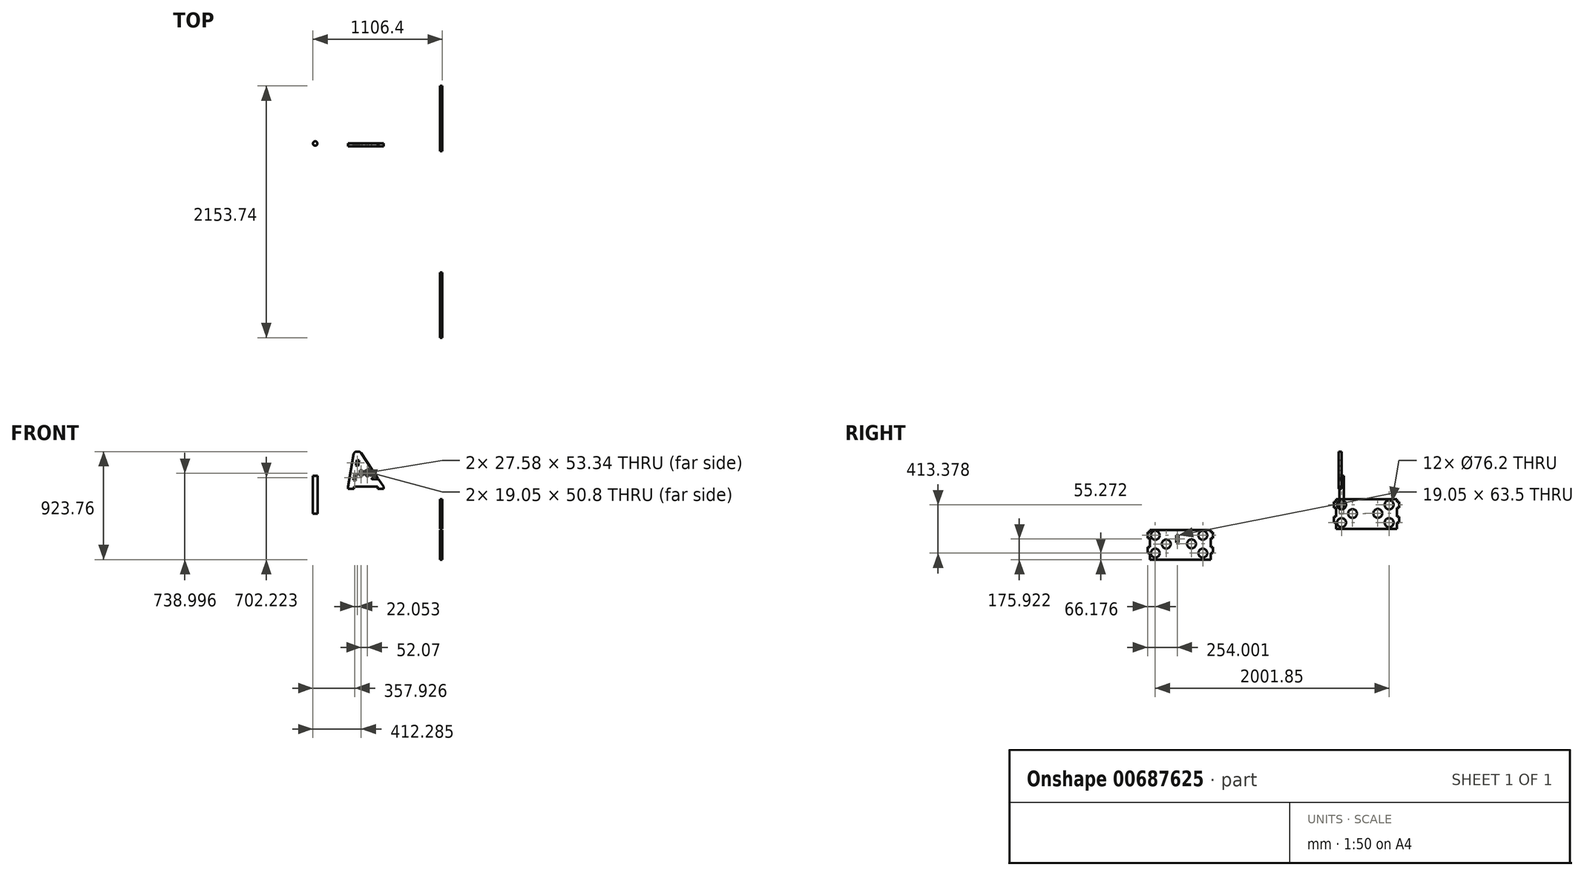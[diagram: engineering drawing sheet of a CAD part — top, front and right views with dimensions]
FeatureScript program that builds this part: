
annotation { "Feature Type Name" : "Feature", "Feature Type Description" : "" }
export const myFeature = defineFeature(function(context is Context, id is Id, definition is map)
    precondition{}
    {
        {
            var Q0;
            Q0=qCreatedBy(makeId("Front.planeOp"),FACE);
            var sketch = newSketch(context, id + "F0", { "sketchPlane" : qUnion([Q0])});
            skLineSegment(sketch, "E0", {"start": v(-737.52, 307.34) * mm, "end": v(-534.32, 307.34) * mm});
            skLineSegment(sketch, "E1", {"start": v(-788.32, 307.34) * mm, "end": v(-739.1, 586.52) * mm});
            skLineSegment(sketch, "E2", {"start": v(-714.08, 607.5) * mm, "end": v(-698.15, 607.5) * mm});
            skLineSegment(sketch, "E3", {"start": v(-677.04, 596.25) * mm, "end": v(-531.9, 379.57) * mm});
            skPoint(sketch, "E4.visualSharp", {"position": v(-735.39, 607.5) * mm});
            skArc(sketch, "E4.filletArc", {"start": v(-714.08, 607.5) * mm, "mid": v(-730.4, 601.57) * mm, "end": v(-739.1, 586.52) * mm});
            skPoint(sketch, "E5.visualSharp", {"position": v(-684.59, 607.5) * mm});
            skArc(sketch, "E5.filletArc", {"start": v(-677.04, 596.25) * mm, "mid": v(-686.19, 604.52) * mm, "end": v(-698.15, 607.5) * mm});
            skLineSegment(sketch, "E6", {"start": v(-712.34, 537.71) * mm, "end": v(-721.16, 487.68) * mm});
            skPoint(sketch, "E7", {"position": v(-738.8, 387.63) * mm});
            skPoint(sketch, "E8", {"position": v(-716.75, 512.7) * mm});
            skLineSegment(sketch, "E9", {"start": v(-715.63, 409.33) * mm, "end": v(-734.4, 412.64) * mm});
            skLineSegment(sketch, "E10.MirrorCS", {"start": v(-5.07, -152.24) * mm, "end": v(-5.07, -55.27) * mm});
            skLineSegment(sketch, "E11", {"start": v(-693.58, 534.4) * mm, "end": v(-712.34, 537.71) * mm});
            skLineSegment(sketch, "E12.MirrorCS", {"start": v(-702.4, 484.38) * mm, "end": v(-721.16, 487.68) * mm});
            skLineSegment(sketch, "E13.MirrorCS", {"start": v(-724.45, 359.3) * mm, "end": v(-743.22, 362.61) * mm});
            skLineSegment(sketch, "E14", {"start": v(-734.4, 412.64) * mm, "end": v(-743.22, 362.61) * mm});
            skPoint(sketch, "E15.orphan", {"position": v(-706.11, 607.5) * mm});
            skLineSegment(sketch, "E16.trimOffspring", {"start": v(-721.16, 487.68) * mm, "end": v(-716.75, 512.7) * mm});
            skPoint(sketch, "E17.orphan", {"position": v(-706.11, 307.34) * mm});
            skLineSegment(sketch, "E18.trimOffspring", {"start": v(-743.22, 362.61) * mm, "end": v(-734.4, 412.64) * mm});
            skLineSegment(sketch, "E19.0", {"start": v(-2.86, 20.83) * mm, "end": v(-2.86, 20.83) * mm});
            skLineSegment(sketch, "E19.1", {"start": v(-738.8, 387.63) * mm, "end": v(-716.75, 512.7) * mm, "construction": true});
            skLineSegment(sketch, "E19.9", {"start": v(-738.8, 387.63) * mm, "end": v(-734.4, 412.64) * mm, "construction": true});
            skLineSegment(sketch, "E20.0", {"start": v(-716.75, 512.7) * mm, "end": v(-712.34, 537.71) * mm, "construction": true});
            skPoint(sketch, "E21", {"position": v(-730.7, 360.4) * mm});
            skLineSegment(sketch, "E22", {"start": v(-693.58, 534.4) * mm, "end": v(-702.4, 484.38) * mm});
            skLineSegment(sketch, "E23", {"start": v(-715.63, 409.33) * mm, "end": v(-724.65, 358.2) * mm});
            skPoint(sketch, "E24.MirrorCS.end.orphan", {"position": v(-718.2, 358.2) * mm});
            skPoint(sketch, "E25.start.orphan", {"position": v(-743.22, 307.34) * mm});
            skPoint(sketch, "E26.end.orphan", {"position": v(-692.42, 288.03) * mm});
            skPoint(sketch, "E27.start.orphan", {"position": v(-576.67, 288.03) * mm});
            skPoint(sketch, "E28.start.orphan", {"position": v(-725.86, 288.3) * mm});
            skPoint(sketch, "E29.start.orphan", {"position": v(-549.17, 288.3) * mm});
            skLineSegment(sketch, "E30", {"start": v(-788.32, 307.34) * mm, "end": v(-788.32, 288.3) * mm});
            skLineSegment(sketch, "E31", {"start": v(-788.32, 288.3) * mm, "end": v(-737.52, 288.3) * mm});
            skLineSegment(sketch, "E32", {"start": v(-737.52, 288.3) * mm, "end": v(-737.52, 307.34) * mm});
            skLineSegment(sketch, "E33", {"start": v(-483.52, 307.34) * mm, "end": v(-483.52, 288.3) * mm});
            skLineSegment(sketch, "E34", {"start": v(-483.52, 288.3) * mm, "end": v(-534.32, 288.3) * mm});
            skLineSegment(sketch, "E35", {"start": v(-534.32, 288.3) * mm, "end": v(-534.32, 307.34) * mm});
            skPoint(sketch, "E36", {"position": v(-531.9, 379.57) * mm});
            skLineSegment(sketch, "E37", {"start": v(-531.9, 379.57) * mm, "end": v(-582.7, 379.57) * mm});
            skLineSegment(sketch, "E38", {"start": v(-585.24, 377.03) * mm, "end": v(-585.24, 374.31) * mm});
            skLineSegment(sketch, "E39", {"start": v(-582.7, 371.77) * mm, "end": v(-526.68, 371.77) * mm});
            skLineSegment(sketch, "E40.trimOffspring", {"start": v(-526.68, 371.77) * mm, "end": v(-483.52, 307.34) * mm});
            skPoint(sketch, "E41.visualSharp", {"position": v(-585.24, 379.57) * mm});
            skArc(sketch, "E41.filletArc", {"start": v(-582.7, 379.57) * mm, "mid": v(-584.5, 378.82) * mm, "end": v(-585.24, 377.03) * mm});
            skPoint(sketch, "E42.visualSharp", {"position": v(-585.24, 371.77) * mm});
            skArc(sketch, "E42.filletArc", {"start": v(-585.24, 374.31) * mm, "mid": v(-584.5, 372.52) * mm, "end": v(-582.7, 371.77) * mm});
            skLineSegment(sketch, "E43", {"start": v(-557.3, 379.57) * mm, "end": v(-585.24, 379.57) * mm});
            skLineSegment(sketch, "E44.top", {"start": v(-665.54, 448.15) * mm, "end": v(-684.59, 448.15) * mm});
            skLineSegment(sketch, "E44.left", {"start": v(-665.54, 397.35) * mm, "end": v(-665.54, 448.15) * mm});
            skLineSegment(sketch, "E44.right", {"start": v(-684.59, 397.35) * mm, "end": v(-684.59, 448.15) * mm});
            skLineSegment(sketch, "E45.trimOffspring", {"start": v(-665.54, 397.35) * mm, "end": v(-684.59, 397.35) * mm});
            skLineSegment(sketch, "E46.top", {"start": v(-613.47, 448.15) * mm, "end": v(-632.52, 448.15) * mm});
            skLineSegment(sketch, "E46.left", {"start": v(-613.47, 397.35) * mm, "end": v(-613.47, 448.15) * mm});
            skLineSegment(sketch, "E46.right", {"start": v(-632.52, 397.35) * mm, "end": v(-632.52, 448.15) * mm});
            skLineSegment(sketch, "E47.trimOffspring", {"start": v(-613.47, 397.35) * mm, "end": v(-632.52, 397.35) * mm});
            skSolve(sketch);
        }
        {
            var Q0;
            Q0=qCreatedBy(makeId("Right.planeOp"),FACE);
            var sketch = newSketch(context, id + "F1", { "sketchPlane" : qUnion([Q0])});
            skLineSegment(sketch, "E48.bottom", {"start": v(0, -58.22) * mm, "end": v(0, -58.22) * mm});
            skLineSegment(sketch, "E48.top", {"start": v(0, 410.3) * mm, "end": v(0, 410.3) * mm});
            skLineSegment(sketch, "E49.bottom", {"start": v(473.58, 198.73) * mm, "end": v(-47.12, 198.73) * mm});
            skLineSegment(sketch, "E49.top", {"start": v(473.58, -55.27) * mm, "end": v(-47.12, -55.27) * mm});
            skLineSegment(sketch, "E49.left", {"start": v(473.58, 198.73) * mm, "end": v(473.58, 50.8) * mm});
            skLineSegment(sketch, "E49.right", {"start": v(-47.12, 198.73) * mm, "end": v(-47.12, 177.8) * mm});
            skPoint(sketch, "E50", {"position": v(-47.12, 186.03) * mm});
            skPoint(sketch, "E51.MirrorP", {"position": v(-47.12, -38.1) * mm});
            skLineSegment(sketch, "E52", {"start": v(473.58, -55.27) * mm, "end": v(473.58, 0) * mm});
            skLineSegment(sketch, "E53", {"start": v(473.58, 0) * mm, "end": v(492.63, 0) * mm});
            skLineSegment(sketch, "E54", {"start": v(492.63, 0) * mm, "end": v(492.63, 50.8) * mm});
            skLineSegment(sketch, "E55", {"start": v(492.63, 50.8) * mm, "end": v(473.58, 50.8) * mm});
            skPoint(sketch, "E56", {"position": v(492.63, 25.4) * mm});
            skLineSegment(sketch, "E57.trimOffspring", {"start": v(473.58, 0) * mm, "end": v(473.58, -55.27) * mm});
            skLineSegment(sketch, "E58", {"start": v(473.58, 127) * mm, "end": v(492.63, 127) * mm});
            skLineSegment(sketch, "E59", {"start": v(492.63, 127) * mm, "end": v(492.63, 177.8) * mm});
            skLineSegment(sketch, "E60", {"start": v(492.63, 177.8) * mm, "end": v(473.58, 177.8) * mm});
            skPoint(sketch, "E61", {"position": v(492.63, 152.4) * mm});
            skLineSegment(sketch, "E62", {"start": v(213.23, 198.73) * mm, "end": v(213.23, -55.27) * mm});
            skLineSegment(sketch, "E63.MirrorCS", {"start": v(-47.12, 127) * mm, "end": v(-66.17, 127) * mm});
            skLineSegment(sketch, "E64.MirrorCS", {"start": v(-66.17, 177.8) * mm, "end": v(-47.12, 177.8) * mm});
            skLineSegment(sketch, "E65.MirrorCS", {"start": v(-66.17, 50.8) * mm, "end": v(-47.12, 50.8) * mm});
            skPoint(sketch, "E66.MirrorP", {"position": v(-66.17, 25.4) * mm});
            skLineSegment(sketch, "E67.MirrorCS", {"start": v(-66.17, 0) * mm, "end": v(-66.17, 50.8) * mm});
            skLineSegment(sketch, "E68.MirrorCS", {"start": v(-47.12, 0) * mm, "end": v(-66.17, 0) * mm});
            skLineSegment(sketch, "E69.MirrorCS", {"start": v(-66.17, 127) * mm, "end": v(-66.17, 177.8) * mm});
            skPoint(sketch, "E70.MirrorP", {"position": v(-66.17, 152.4) * mm});
            skLineSegment(sketch, "E71.trimOffspring", {"start": v(-47.12, 127) * mm, "end": v(-47.12, 50.8) * mm});
            skLineSegment(sketch, "E72.trimOffspring", {"start": v(-47.12, 0) * mm, "end": v(-47.12, -55.27) * mm});
            skLineSegment(sketch, "E73", {"start": v(492.63, 152.4) * mm, "end": v(-66.17, 152.4) * mm});
            skCircle(sketch, "E74", {"center": v(406.91, 152.4) * mm, "radius": 38.1 * mm});
            skCircle(sketch, "E75", {"center": v(0, 152.4) * mm, "radius": 38.1 * mm});
            skCircle(sketch, "E76", {"center": v(406.91, 0) * mm, "radius": 38.1 * mm});
            skCircle(sketch, "E77", {"center": v(0, 0) * mm, "radius": 38.1 * mm});
            skCircle(sketch, "E78", {"center": v(94.07, 77.72) * mm, "radius": 38.1 * mm});
            skCircle(sketch, "E79", {"center": v(310.03, 78.89) * mm, "radius": 38.1 * mm});
            skLineSegment(sketch, "E80.bottom", {"start": v(-1594.93, -319.2) * mm, "end": v(-1594.93, -319.2) * mm});
            skLineSegment(sketch, "E81.bottom", {"start": v(-1121.36, -62.25) * mm, "end": v(-1642.06, -62.25) * mm});
            skLineSegment(sketch, "E81.top", {"start": v(-1121.36, -316.25) * mm, "end": v(-1642.06, -316.25) * mm});
            skLineSegment(sketch, "E81.left", {"start": v(-1121.36, -62.25) * mm, "end": v(-1121.36, -210.18) * mm});
            skLineSegment(sketch, "E81.right", {"start": v(-1642.06, -62.25) * mm, "end": v(-1642.06, -83.18) * mm});
            skPoint(sketch, "E82", {"position": v(-1642.06, -74.95) * mm});
            skPoint(sketch, "E83.MirrorP", {"position": v(-1642.06, -299.08) * mm});
            skLineSegment(sketch, "E84", {"start": v(-1121.36, -316.25) * mm, "end": v(-1121.36, -260.98) * mm});
            skLineSegment(sketch, "E85", {"start": v(-1121.36, -260.98) * mm, "end": v(-1102.3, -260.98) * mm});
            skLineSegment(sketch, "E86", {"start": v(-1102.3, -260.98) * mm, "end": v(-1102.3, -210.18) * mm});
            skLineSegment(sketch, "E87", {"start": v(-1102.3, -210.18) * mm, "end": v(-1121.36, -210.18) * mm});
            skPoint(sketch, "E88", {"position": v(-1102.3, -235.58) * mm});
            skLineSegment(sketch, "E89.trimOffspring", {"start": v(-1121.36, -260.98) * mm, "end": v(-1121.36, -316.25) * mm});
            skLineSegment(sketch, "E90", {"start": v(-1121.36, -133.98) * mm, "end": v(-1102.3, -133.98) * mm});
            skLineSegment(sketch, "E91", {"start": v(-1102.3, -133.98) * mm, "end": v(-1102.3, -83.18) * mm});
            skLineSegment(sketch, "E92", {"start": v(-1102.3, -83.18) * mm, "end": v(-1121.36, -83.18) * mm});
            skPoint(sketch, "E93", {"position": v(-1102.3, -108.58) * mm});
            skLineSegment(sketch, "E94", {"start": v(-1381.7, -62.25) * mm, "end": v(-1381.7, -316.25) * mm});
            skLineSegment(sketch, "E95.MirrorCS", {"start": v(-1642.06, -133.98) * mm, "end": v(-1661.1, -133.98) * mm});
            skLineSegment(sketch, "E96.MirrorCS", {"start": v(-1661.1, -83.18) * mm, "end": v(-1642.06, -83.18) * mm});
            skLineSegment(sketch, "E97.MirrorCS", {"start": v(-1661.1, -210.18) * mm, "end": v(-1642.06, -210.18) * mm});
            skPoint(sketch, "E98.MirrorP", {"position": v(-1661.1, -235.58) * mm});
            skLineSegment(sketch, "E99.MirrorCS", {"start": v(-1661.1, -260.98) * mm, "end": v(-1661.1, -210.18) * mm});
            skLineSegment(sketch, "E100.MirrorCS", {"start": v(-1642.06, -260.98) * mm, "end": v(-1661.1, -260.98) * mm});
            skLineSegment(sketch, "E101.MirrorCS", {"start": v(-1661.1, -133.98) * mm, "end": v(-1661.1, -83.18) * mm});
            skPoint(sketch, "E102.MirrorP", {"position": v(-1661.1, -108.58) * mm});
            skLineSegment(sketch, "E103.trimOffspring", {"start": v(-1642.06, -133.98) * mm, "end": v(-1642.06, -210.18) * mm});
            skLineSegment(sketch, "E104.trimOffspring", {"start": v(-1642.06, -260.98) * mm, "end": v(-1642.06, -316.25) * mm});
            skCircle(sketch, "E105", {"center": v(-1188.02, -108.58) * mm, "radius": 38.1 * mm});
            skCircle(sketch, "E106", {"center": v(-1594.93, -108.58) * mm, "radius": 38.1 * mm});
            skCircle(sketch, "E107", {"center": v(-1188.02, -260.98) * mm, "radius": 38.1 * mm});
            skCircle(sketch, "E108", {"center": v(-1594.93, -260.98) * mm, "radius": 38.1 * mm});
            skCircle(sketch, "E109", {"center": v(-1500.86, -183.26) * mm, "radius": 38.1 * mm});
            skCircle(sketch, "E110", {"center": v(-1284.9, -182.1) * mm, "radius": 38.1 * mm});
            skLineSegment(sketch, "E111", {"start": v(-1416.63, -108.58) * mm, "end": v(-1416.63, -172.08) * mm});
            skLineSegment(sketch, "E112", {"start": v(-1416.63, -172.08) * mm, "end": v(-1397.58, -172.08) * mm});
            skLineSegment(sketch, "E113", {"start": v(-1397.58, -172.08) * mm, "end": v(-1397.58, -108.58) * mm});
            skLineSegment(sketch, "E114.trimOffspring", {"start": v(-1397.58, -108.58) * mm, "end": v(-1416.63, -108.58) * mm});
            skSolve(sketch);
        }
        {
            var Q0;
            Q0=qCreatedBy(makeId("Front.planeOp"),FACE);
            var sketch = newSketch(context, id + "F2", { "sketchPlane" : qUnion([Q0])});
            skLineSegment(sketch, "E115.bottom", {"start": v(-1087.35, 400.45) * mm, "end": v(-1068.21, 400.45) * mm});
            skLineSegment(sketch, "E115.top", {"start": v(-1087.35, 77.8) * mm, "end": v(-1068.21, 77.8) * mm});
            skLineSegment(sketch, "E115.left", {"start": v(-1087.35, 400.45) * mm, "end": v(-1087.35, 77.8) * mm});
            skLineSegment(sketch, "E115.right", {"start": v(-1068.21, 400.45) * mm, "end": v(-1068.21, 77.8) * mm});
            skSolve(sketch);
        }
        {
            var Q0;
            Q0=makeQuery(id+"F2.imprint","IMPRINT",FACE,{"disambiguationData":[TD([[makeQuery(id+"F2.imprint","IMPRINT",EDGE,{"derivedFrom":sQuery(id+"F2.wireOp",EDGE,"E115.bottom")}),-1.0]])]});
            var Q1;
            Q1=sQuery(id+"F2.wireOp",EDGE,"E115.right");
            revolve(context, id + "F3", {"entities" : qUnion([Q0]), "axis" : qUnion([Q1]), "revolveType" : RevolveType.FULL});
        }
        {
            var Q0;
            Q0 = qSketchRegion(id + "F0", true);
            extrude(context, id + "F4", {"entities" : qUnion([Q0]), "depth" : 25.4 * mm, "offsetDistance" : 25.4 * mm});
        }
        {
            var Q0;
            Q0 = qSketchRegion(id + "F1", true);
            extrude(context, id + "F5", {"entities" : qUnion([Q0]), "depth" : 19.05 * mm, "offsetDistance" : 25.4 * mm});
        }
    });
